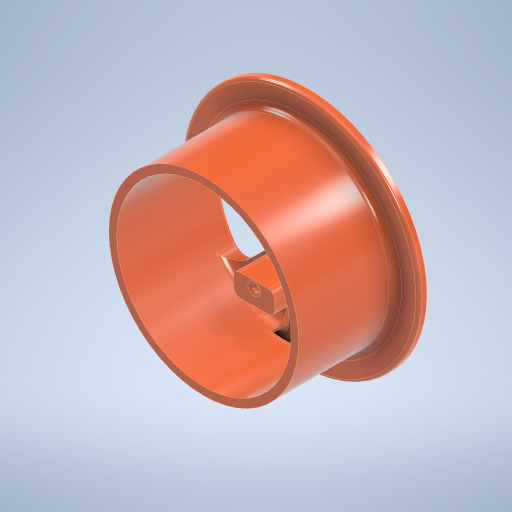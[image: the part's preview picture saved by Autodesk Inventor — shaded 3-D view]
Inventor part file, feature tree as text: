
AUTODESK INVENTOR PART (.ipt)
format: ipt  version: 2023.2 (Build 272271000, 271)  size: 676,352 bytes
history: native  units: mm
features: fillet x9, sketch x6, extrude x5, hole x1
ambient origin geometry x8: Origin, YZ Plane, XZ Plane, XY Plane, X Axis, Y Axis, Z Axis, Center Point
bodies: Solid1 (feature_tree)
feature tree (21):
  extrude  "Extrusion1"  Depth=2.5mm
  extrude  "Extrusion2"  Depth=2.5mm TaperAngle=0.0deg
  extrude  "Extrusion3"  Depth=10.0mm
  hole  "Hole1"  [1 undecoded]
  extrude  "Extrusion5"  Depth=55.0mm
  fillet  "Fillet1"  Radius=17.1mm
  extrude  "Extrusion6"  Depth=1.0mm
  fillet  "Fillet2"  Radius=5.0mm
  fillet  "Fillet3"  Radius=5.0mm
  fillet  "Fillet4"  Radius=25.1mm
  fillet  "Fillet5"  Radius=2.0mm
  fillet  "Fillet7"  Radius=2.0mm
  fillet  "Fillet8"  Radius=5.0mm
  fillet  "Fillet9"  Radius=8.5mm
  fillet  "Fillet10"  Radius=10.0mm
  sketch  "Sketch1"  dims[d0=60.0mm d1=2.5mm]
  sketch  "Sketch2"  dims[d2=33.0mm d3=0.0mm d5=2.5mm d6=0.0mm]
  sketch  "Sketch3"  dims[d7=55.0mm d8=10.0mm]
  sketch  "Sketch4"  dims[d9=16.8mm d10=6.4mm]
  sketch  "Sketch6"  dims[d11=13.0mm d12=55.0mm d14=16.8mm d15=6.4mm d16=13.0mm d17=17.1mm d18=0.0mm]
  sketch  "Sketch7"  dims[d19=27.8mm d20=8.7mm d21=2.0mm d22=6.0mm d23=4.0mm d24=2.0mm d25=90.0deg d26=7.0mm d27=0.0mm d32=5.0mm d33=5.0mm d34=25.1mm d35=0.0mm d36=2.0mm d37=2.0mm d38=5.0mm d39=8.5mm d40=10.0mm d41=0.0mm d42=4.0mm d43=2.0mm d44=2.0mm d45=2.0mm d47=1.0mm d48=1.0mm d49=2.0mm d50=1.0mm]
note: 1 required parameter value undecoded (feature->parameter linkage not recoverable at this tier; creation-order binding heuristic only, values carry confidence <= 0.55)
